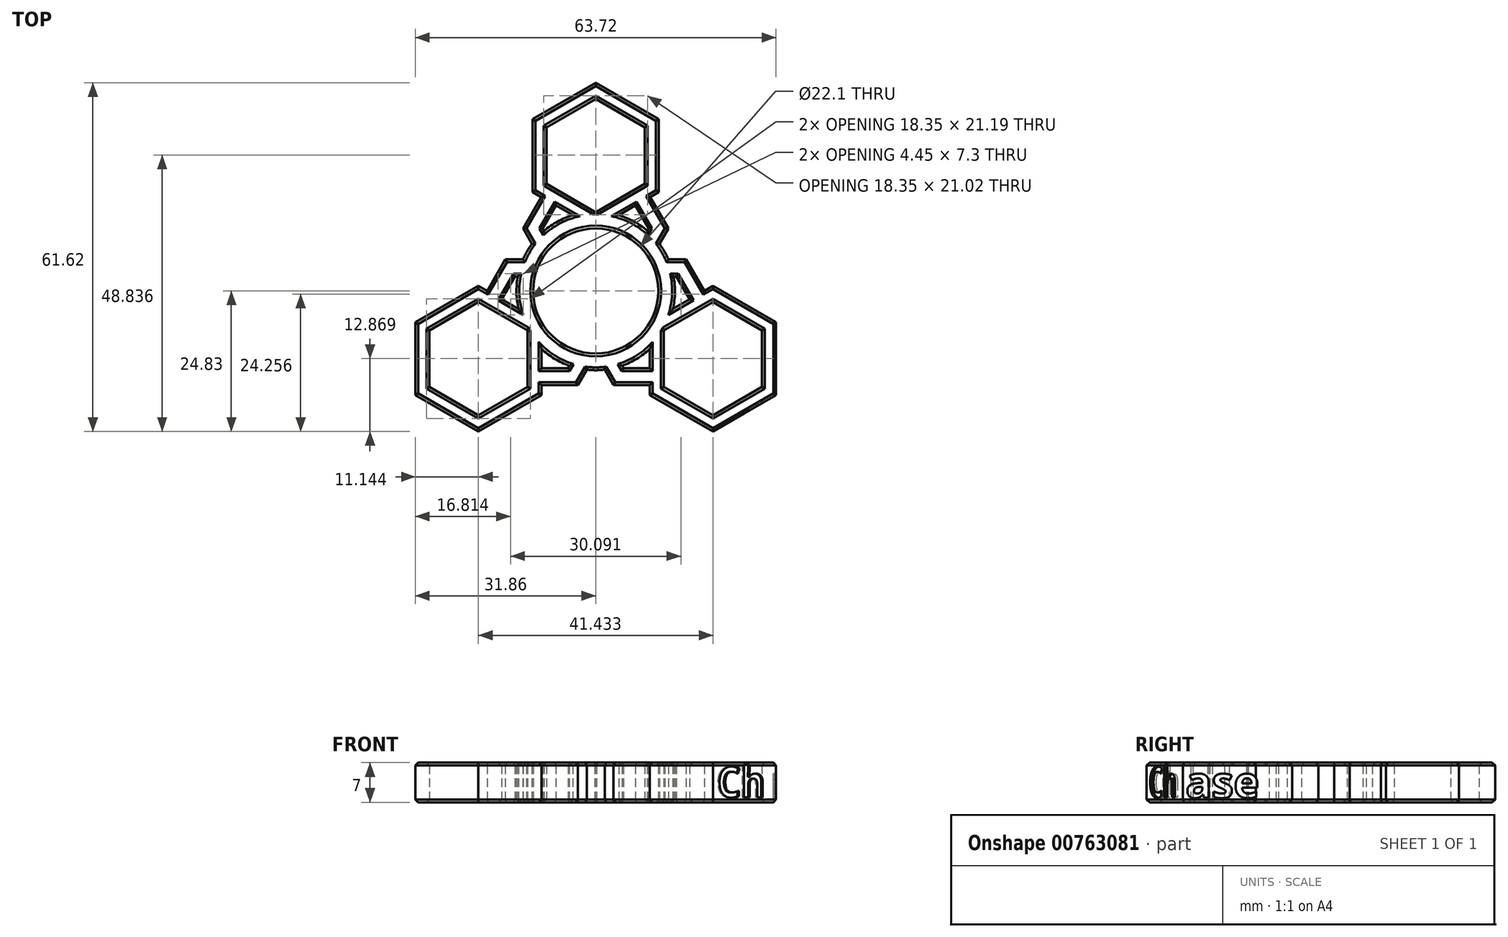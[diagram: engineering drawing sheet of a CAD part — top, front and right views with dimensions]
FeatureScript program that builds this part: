
annotation { "Feature Type Name" : "Feature", "Feature Type Description" : "" }
export const myFeature = defineFeature(function(context is Context, id is Id, definition is map)
    precondition{}
    {
        {
            var Q0;
            Q0=qCreatedBy(makeId("Top.planeOp"),FACE);
            var sketch = newSketch(context, id + "F0", { "sketchPlane" : qUnion([Q0])});
            skCircle(sketch, "E0", {"center": v(0, 0) * mm, "radius": 11.05 * mm});
            skCircle(sketch, "E1.cCircle", {"center": v(0, 23.92) * mm, "radius": 10.02 * mm, "construction": true});
            skLineSegment(sketch, "E1.0", {"start": v(0, 33.94) * mm, "end": v(8.68, 28.93) * mm});
            skLineSegment(sketch, "E1.1", {"start": v(8.67, 28.93) * mm, "end": v(8.68, 18.91) * mm});
            skLineSegment(sketch, "E1.2", {"start": v(8.67, 18.91) * mm, "end": v(0, 13.9) * mm});
            skLineSegment(sketch, "E1.3", {"start": v(0, 13.9) * mm, "end": v(-8.67, 18.91) * mm});
            skLineSegment(sketch, "E1.4", {"start": v(-8.67, 18.91) * mm, "end": v(-8.68, 28.93) * mm});
            skLineSegment(sketch, "E1.5", {"start": v(-8.67, 28.93) * mm, "end": v(0, 33.94) * mm});
            skCircle(sketch, "E2.cCircle", {"center": v(0, 11.05) * mm, "radius": 9.36 * mm, "construction": true});
            skLineSegment(sketch, "E2.0", {"start": v(9.36, 11.05) * mm, "end": v(4.68, 2.95) * mm});
            skLineSegment(sketch, "E2.1", {"start": v(4.68, 2.95) * mm, "end": v(-4.68, 2.95) * mm});
            skLineSegment(sketch, "E2.2", {"start": v(-4.68, 2.95) * mm, "end": v(-9.36, 11.05) * mm});
            skLineSegment(sketch, "E2.3", {"start": v(-9.36, 11.05) * mm, "end": v(-4.68, 19.15) * mm});
            skLineSegment(sketch, "E2.4", {"start": v(-4.68, 19.15) * mm, "end": v(4.68, 19.15) * mm});
            skLineSegment(sketch, "E2.5", {"start": v(4.68, 19.15) * mm, "end": v(9.36, 11.05) * mm});
            skLineSegment(sketch, "E3", {"start": v(0, 11.05) * mm, "end": v(30.07, 11.05) * mm, "construction": true});
            skLineSegment(sketch, "E4.0", {"start": v(-6.4, -0.05) * mm, "end": v(-12.82, 11.05) * mm});
            skLineSegment(sketch, "E4.1", {"start": v(-6.4, 22.15) * mm, "end": v(6.4, 22.15) * mm});
            skLineSegment(sketch, "E4.2", {"start": v(6.4, 22.15) * mm, "end": v(12.82, 11.05) * mm});
            skLineSegment(sketch, "E4.3", {"start": v(-12.82, 11.05) * mm, "end": v(-6.4, 22.15) * mm});
            skLineSegment(sketch, "E4.4", {"start": v(12.82, 11.05) * mm, "end": v(6.4, -0.05) * mm});
            skLineSegment(sketch, "E4.5", {"start": v(6.4, -0.05) * mm, "end": v(-6.4, -0.05) * mm});
            skCircle(sketch, "E5", {"center": v(0, 0) * mm, "radius": 14 * mm});
            skCircle(sketch, "E6.cCircle", {"center": v(0, 23.92) * mm, "radius": 12.87 * mm, "construction": true});
            skLineSegment(sketch, "E6.0", {"start": v(0, 11.05) * mm, "end": v(-11.15, 17.49) * mm});
            skLineSegment(sketch, "E6.1", {"start": v(-11.15, 17.49) * mm, "end": v(-11.15, 30.36) * mm});
            skLineSegment(sketch, "E6.2", {"start": v(-11.15, 30.36) * mm, "end": v(0, 36.8) * mm});
            skLineSegment(sketch, "E6.3", {"start": v(0, 36.8) * mm, "end": v(11.15, 30.36) * mm});
            skLineSegment(sketch, "E6.4", {"start": v(11.15, 30.36) * mm, "end": v(11.15, 17.49) * mm});
            skLineSegment(sketch, "E6.5", {"start": v(11.15, 17.49) * mm, "end": v(0, 11.05) * mm});
            skSolve(sketch);
        }
        {
            var Q0;
            {var subQ5=sQuery(id+"F0.wireOp",EDGE,"E1.0");Q0=makeQuery(id+"F0.imprint","IMPRINT",FACE,{"disambiguationData":[TD([[makeQuery(id+"F0.imprint","IMPRINT",EDGE,{"derivedFrom":subQ5}),1.0]])]});}
            var Q1;
            {var subQ1=sQuery(id+"F0.wireOp",EDGE,"E1.3");var subQ5=sQuery(id+"F0.wireOp",EDGE,"E1.4");var subQ6=makeQuery(id+"F0.imprint","INTERSECT",VERTEX,{"derivedFrom":[subQ1,subQ5]});Q1=makeQuery(id+"F0.imprint","IMPRINT",FACE,{"disambiguationData":[TD([[makeQuery(id+"F0.imprint","IMPRINT",EDGE,{"disambiguationData":[TD([[subQ6,1.0]])],"derivedFrom":subQ1}),1.0]])]});}
            var Q2;
            {var subQ1=sQuery(id+"F0.wireOp",EDGE,"E1.2");var subQ6=sQuery(id+"F0.wireOp",EDGE,"E1.3");var subQ13=makeQuery(id+"F0.imprint","INTERSECT",VERTEX,{"derivedFrom":[subQ1,subQ6]});Q2=makeQuery(id+"F0.imprint","IMPRINT",FACE,{"disambiguationData":[TD([[makeQuery(id+"F0.imprint","IMPRINT",EDGE,{"disambiguationData":[TD([[subQ13,1.0]])],"derivedFrom":subQ1}),1.0]])]});}
            var Q3;
            {var subQ3=sQuery(id+"F0.wireOp",EDGE,"E1.1");var subQ5=sQuery(id+"F0.wireOp",EDGE,"E1.2");var subQ6=makeQuery(id+"F0.imprint","INTERSECT",VERTEX,{"derivedFrom":[subQ3,subQ5]});Q3=makeQuery(id+"F0.imprint","IMPRINT",FACE,{"disambiguationData":[TD([[makeQuery(id+"F0.imprint","IMPRINT",EDGE,{"disambiguationData":[TD([[subQ6,1.0]])],"derivedFrom":subQ3}),1.0]])]});}
            var Q4;
            {var subQ5=sQuery(id+"F0.wireOp",EDGE,"E2.5");var subQ6=sQuery(id+"F0.wireOp",EDGE,"E2.0");var subQ7=makeQuery(id+"F0.imprint","INTERSECT",VERTEX,{"derivedFrom":[subQ6,subQ5]});Q4=makeQuery(id+"F0.imprint","IMPRINT",FACE,{"disambiguationData":[TD([[makeQuery(id+"F0.imprint","IMPRINT",EDGE,{"disambiguationData":[TD([[subQ7,-1.0]])],"derivedFrom":subQ6}),1.0]])]});}
            var Q5;
            {var subQ0=sQuery(id+"F0.wireOp",EDGE,"E2.0");var subQ1=sQuery(id+"F0.wireOp",EDGE,"E0");var subQ2=makeQuery(id+"F0.imprint","INTERSECT",VERTEX,{"derivedFrom":[subQ1,subQ0]});Q5=makeQuery(id+"F0.imprint","IMPRINT",FACE,{"disambiguationData":[TD([[makeQuery(id+"F0.imprint","IMPRINT",EDGE,{"disambiguationData":[TD([[subQ2,1.0]])],"derivedFrom":subQ1}),-1.0]])]});}
            var Q6;
            {var subQ1=sQuery(id+"F0.wireOp",EDGE,"E0");var subQ3=sQuery(id+"F0.wireOp",EDGE,"E2.0");var subQ4=makeQuery(id+"F0.imprint","INTERSECT",VERTEX,{"derivedFrom":[subQ1,subQ3]});Q6=makeQuery(id+"F0.imprint","IMPRINT",FACE,{"disambiguationData":[TD([[makeQuery(id+"F0.imprint","IMPRINT",EDGE,{"disambiguationData":[TD([[subQ4,1.0]])],"derivedFrom":subQ3}),-1.0]])]});}
            var Q7;
            {var subQ1=sQuery(id+"F0.wireOp",EDGE,"E0");var subQ3=sQuery(id+"F0.wireOp",EDGE,"E2.2");var subQ4=makeQuery(id+"F0.imprint","INTERSECT",VERTEX,{"derivedFrom":[subQ1,subQ3]});Q7=makeQuery(id+"F0.imprint","IMPRINT",FACE,{"disambiguationData":[TD([[makeQuery(id+"F0.imprint","IMPRINT",EDGE,{"disambiguationData":[TD([[subQ4,-1.0]])],"derivedFrom":subQ3}),-1.0]])]});}
            var Q8;
            {var subQ0=sQuery(id+"F0.wireOp",EDGE,"E6.5");var subQ1=sQuery(id+"F0.wireOp",EDGE,"E5");var subQ2=makeQuery(id+"F0.imprint","INTERSECT",VERTEX,{"derivedFrom":[subQ1,subQ0]});Q8=makeQuery(id+"F0.imprint","IMPRINT",FACE,{"disambiguationData":[TD([[makeQuery(id+"F0.imprint","IMPRINT",EDGE,{"disambiguationData":[TD([[subQ2,-1.0]])],"derivedFrom":subQ1}),1.0]])]});}
            var Q9;
            {var subQ0=sQuery(id+"F0.wireOp",EDGE,"E4.4");var subQ1=sQuery(id+"F0.wireOp",EDGE,"E0");var subQ2=makeQuery(id+"F0.imprint","INTERSECT",VERTEX,{"derivedFrom":[subQ1,subQ0]});Q9=makeQuery(id+"F0.imprint","IMPRINT",FACE,{"disambiguationData":[TD([[makeQuery(id+"F0.imprint","IMPRINT",EDGE,{"disambiguationData":[TD([[subQ2,1.0]])],"derivedFrom":subQ1}),-1.0]])]});}
            var Q10;
            {var subQ0=sQuery(id+"F0.wireOp",EDGE,"E2.2");var subQ1=sQuery(id+"F0.wireOp",EDGE,"E0");var subQ2=makeQuery(id+"F0.imprint","INTERSECT",VERTEX,{"derivedFrom":[subQ1,subQ0]});Q10=makeQuery(id+"F0.imprint","IMPRINT",FACE,{"disambiguationData":[TD([[makeQuery(id+"F0.imprint","IMPRINT",EDGE,{"disambiguationData":[TD([[subQ2,-1.0]])],"derivedFrom":subQ1}),-1.0]])]});}
            var Q11;
            {var subQ0=sQuery(id+"F0.wireOp",EDGE,"E2.3");var subQ1=sQuery(id+"F0.wireOp",EDGE,"E2.2");var subQ2=makeQuery(id+"F0.imprint","INTERSECT",VERTEX,{"derivedFrom":[subQ1,subQ0]});Q11=makeQuery(id+"F0.imprint","IMPRINT",FACE,{"disambiguationData":[TD([[makeQuery(id+"F0.imprint","IMPRINT",EDGE,{"disambiguationData":[TD([[subQ2,1.0]])],"derivedFrom":subQ1}),1.0]])]});}
            var Q12;
            {var subQ0=sQuery(id+"F0.wireOp",EDGE,"E5");var subQ1=sQuery(id+"F0.wireOp",EDGE,"E1.3");var subQ2=makeQuery(id+"F0.imprint","INTERSECT",VERTEX,{"derivedFrom":[subQ1,subQ0]});Q12=makeQuery(id+"F0.imprint","IMPRINT",FACE,{"disambiguationData":[TD([[makeQuery(id+"F0.imprint","IMPRINT",EDGE,{"disambiguationData":[TD([[subQ2,-1.0]])],"derivedFrom":subQ1}),1.0]])]});}
            var Q13;
            {var subQ0=sQuery(id+"F0.wireOp",EDGE,"E2.3");var subQ1=sQuery(id+"F0.wireOp",EDGE,"E1.3");var subQ2=makeQuery(id+"F0.imprint","INTERSECT",VERTEX,{"derivedFrom":[subQ1,subQ0]});Q13=makeQuery(id+"F0.imprint","IMPRINT",FACE,{"disambiguationData":[TD([[makeQuery(id+"F0.imprint","IMPRINT",EDGE,{"disambiguationData":[TD([[subQ2,-1.0]])],"derivedFrom":subQ1}),1.0]])]});}
            var Q14;
            {var subQ0=sQuery(id+"F0.wireOp",EDGE,"E4.2");var subQ1=sQuery(id+"F0.wireOp",EDGE,"E1.2");var subQ2=makeQuery(id+"F0.imprint","INTERSECT",VERTEX,{"derivedFrom":[subQ1,subQ0]});Q14=makeQuery(id+"F0.imprint","IMPRINT",FACE,{"disambiguationData":[TD([[makeQuery(id+"F0.imprint","IMPRINT",EDGE,{"disambiguationData":[TD([[subQ2,-1.0]])],"derivedFrom":subQ1}),1.0]])]});}
            var Q15;
            {var subQ0=sQuery(id+"F0.wireOp",EDGE,"E2.5");var subQ1=sQuery(id+"F0.wireOp",EDGE,"E1.2");var subQ2=makeQuery(id+"F0.imprint","INTERSECT",VERTEX,{"derivedFrom":[subQ1,subQ0]});Q15=makeQuery(id+"F0.imprint","IMPRINT",FACE,{"disambiguationData":[TD([[makeQuery(id+"F0.imprint","IMPRINT",EDGE,{"disambiguationData":[TD([[subQ2,-1.0]])],"derivedFrom":subQ1}),1.0]])]});}
            extrude(context, id + "F1", {"entities" : qUnion([Q0, Q1, Q2, Q3, Q4, Q5, Q6, Q7, Q8, Q9, Q10, Q11, Q12, Q13, Q14, Q15]), "depth" : 7 * mm, "offsetDistance" : 25 * mm});
        }
        {
            var Q0;
            Q0=qCreatedBy(makeId("Right.planeOp"),FACE);
            var sketch = newSketch(context, id + "F2", { "sketchPlane" : qUnion([Q0])});
            skLineSegment(sketch, "E7", {"start": v(0, 0) * mm, "end": v(0, 30.07) * mm});
            skSolve(sketch);
        }
        {
            var Q0;
            Q0=makeQuery(id+"F1.opExtrude","SWEPT_BODY",BODY,{"disambiguationData":[OSD([sQuery(id+"F0.wireOp",EDGE,"E0"),sQuery(id+"F0.wireOp",EDGE,"E1.0"),sQuery(id+"F0.wireOp",EDGE,"E1.1"),sQuery(id+"F0.wireOp",EDGE,"E1.2"),sQuery(id+"F0.wireOp",EDGE,"E1.3"),sQuery(id+"F0.wireOp",EDGE,"E1.4"),sQuery(id+"F0.wireOp",EDGE,"E1.5"),sQuery(id+"F0.wireOp",EDGE,"E2.0"),sQuery(id+"F0.wireOp",EDGE,"E2.2"),sQuery(id+"F0.wireOp",EDGE,"E2.3"),sQuery(id+"F0.wireOp",EDGE,"E2.5"),sQuery(id+"F0.wireOp",EDGE,"E4.0"),sQuery(id+"F0.wireOp",EDGE,"E4.2"),sQuery(id+"F0.wireOp",EDGE,"E4.3"),sQuery(id+"F0.wireOp",EDGE,"E4.4"),sQuery(id+"F0.wireOp",EDGE,"E5"),sQuery(id+"F0.wireOp",EDGE,"E6.0"),sQuery(id+"F0.wireOp",EDGE,"E6.1"),sQuery(id+"F0.wireOp",EDGE,"E6.2"),sQuery(id+"F0.wireOp",EDGE,"E6.3"),sQuery(id+"F0.wireOp",EDGE,"E6.4"),sQuery(id+"F0.wireOp",EDGE,"E6.5")])]});
            var Q1;
            Q1=sQuery(id+"F2.wireOp",EDGE,"E7");
            circularPattern(context, id + "F3", {"operationType" : NewBodyOperationType.ADD, "entities" : qUnion([Q0]), "axis" : qUnion([Q1]), "angle" : 360 * degree, "instanceCount" : 3, "equalSpace" : true});
        }
        {
            var Q0;
            Q0=makeQuery(id+"F3.opPattern","COPY",FACE,{"derivedFrom":makeQuery(id+"F1.opExtrude","SWEPT_FACE",FACE,{"disambiguationData":[OSD([sQuery(id+"F0.wireOp",EDGE,"E6.3")])]}),"instanceName":"2"});
            var sketch = newSketch(context, id + "F4", { "sketchPlane" : qUnion([Q0])});
            skText(sketch, "E8", { "text": "Ch", "fontName": "OpenSans-Bold.ttf"});
            const initialGuessF4  = {"E8": [0.00642, 0.00086, 1, 0, 0.00546]};
            skSetInitialGuess(sketch, initialGuessF4);
            skSolve(sketch);
        }
        {
            var Q0;
            Q0=makeQuery(id+"F3.opPattern","COPY",FACE,{"derivedFrom":makeQuery(id+"F1.opExtrude","SWEPT_FACE",FACE,{"disambiguationData":[OSD([sQuery(id+"F0.wireOp",EDGE,"E6.2")])]}),"instanceName":"2"});
            var sketch = newSketch(context, id + "F5", { "sketchPlane" : qUnion([Q0])});
            skText(sketch, "E9", { "text": "ase", "fontName": "OpenSans-Bold.ttf"});
            const initialGuessF5  = {"E9": [-0.01792, 0.00078, 1, 0, 0.00555]};
            skSetInitialGuess(sketch, initialGuessF5);
            skSolve(sketch);
        }
        {
            var Q0;
            Q0=qSketchRegion(id+"F4",true);
            extrude(context, id + "F6", {"entities" : qUnion([Q0]), "operationType" : NewBodyOperationType.REMOVE, "oppositeDirection" : true, "depth" : .5 * mm, "offsetDistance" : 25 * mm});
        }
        {
            var Q0;
            Q0=qSketchRegion(id+"F5",true);
            extrude(context, id + "F7", {"entities" : qUnion([Q0]), "operationType" : NewBodyOperationType.REMOVE, "oppositeDirection" : true, "depth" : .5 * mm, "offsetDistance" : 25 * mm});
        }
        {
            var Q0;
            Q0=makeQuery(id+"F3.opPattern","COPY",EDGE,{"derivedFrom":makeQuery(id+"F1.opExtrude","CAP_EDGE",EDGE,{"disambiguationData":[OSD([sQuery(id+"F0.wireOp",EDGE,"E6.1")])],"isStart":false}),"instanceName":"2"});
            var Q1;
            Q1=makeQuery(id+"F3.opPattern","COPY",EDGE,{"derivedFrom":makeQuery(id+"F1.opExtrude","CAP_EDGE",EDGE,{"disambiguationData":[OSD([sQuery(id+"F0.wireOp",EDGE,"E6.2")])],"isStart":false}),"instanceName":"2"});
            var Q2;
            Q2=makeQuery(id+"F3.opPattern","COPY",EDGE,{"derivedFrom":makeQuery(id+"F1.opExtrude","CAP_EDGE",EDGE,{"disambiguationData":[OSD([sQuery(id+"F0.wireOp",EDGE,"E6.3")])],"isStart":false}),"instanceName":"2"});
            var Q3;
            Q3=makeQuery(id+"F3.opPattern","COPY",EDGE,{"derivedFrom":makeQuery(id+"F1.opExtrude","CAP_EDGE",EDGE,{"disambiguationData":[OSD([sQuery(id+"F0.wireOp",EDGE,"E6.4")])],"isStart":false}),"instanceName":"2"});
            var Q4;
            {var subQ0=sQuery(id+"F0.wireOp",EDGE,"E6.5");Q4=makeQuery(id+"F3.opPattern","COPY",EDGE,{"derivedFrom":makeQuery(id+"F1.opExtrude","CAP_EDGE",EDGE,{"disambiguationData":[OSD([subQ0]),TDD([makeQuery(id+"F0.imprint","IMPRINT",EDGE,{"disambiguationData":[TD([[makeQuery(id+"F0.imprint","INTERSECT",VERTEX,{"derivedFrom":[sQuery(id+"F0.wireOp",EDGE,"E6.4"),subQ0]}),-1.0]])],"derivedFrom":subQ0})])],"isStart":false}),"instanceName":"2"});}
            var Q5;
            Q5=makeQuery(id+"F3.opPattern","COPY",EDGE,{"derivedFrom":makeQuery(id+"F1.opExtrude","CAP_EDGE",EDGE,{"disambiguationData":[OSD([sQuery(id+"F0.wireOp",EDGE,"E4.2")])],"isStart":false}),"instanceName":"2"});
            var Q6;
            Q6=makeQuery(id+"F3.opPattern","COPY",EDGE,{"derivedFrom":makeQuery(id+"F1.opExtrude","CAP_EDGE",EDGE,{"disambiguationData":[OSD([sQuery(id+"F0.wireOp",EDGE,"E4.4")])],"isStart":false}),"instanceName":"2"});
            var Q7;
            {var subQ0=sQuery(id+"F0.wireOp",EDGE,"E4.0");var subQ1=sQuery(id+"F0.wireOp",EDGE,"E5");var subQ4=makeQuery(id+"F0.imprint","IMPRINT",EDGE,{"disambiguationData":[TD([[makeQuery(id+"F0.imprint","INTERSECT",VERTEX,{"derivedFrom":[subQ0,subQ1]}),-1.0]])],"derivedFrom":subQ1});Q7=makeQuery(id+"F3.boolean.opBoolean","SPLIT",EDGE,{"disambiguationData":[TD([makeQuery(id+"F3.opPattern","COPY",FACE,{"derivedFrom":makeQuery(id+"F1.opExtrude","SWEPT_FACE",FACE,{"disambiguationData":[OSD([subQ0])]}),"instanceName":"1"})])],"derivedFrom":makeQuery(id+"F1.opExtrude","CAP_EDGE",EDGE,{"disambiguationData":[OSD([subQ1]),TDD([subQ4])],"isStart":false})});}
            var Q8;
            Q8=makeQuery(id+"F3.opPattern","COPY",EDGE,{"derivedFrom":makeQuery(id+"F1.opExtrude","CAP_EDGE",EDGE,{"disambiguationData":[OSD([sQuery(id+"F0.wireOp",EDGE,"E4.0")])],"isStart":false}),"instanceName":"1"});
            var Q9;
            Q9=makeQuery(id+"F3.opPattern","COPY",EDGE,{"derivedFrom":makeQuery(id+"F1.opExtrude","CAP_EDGE",EDGE,{"disambiguationData":[OSD([sQuery(id+"F0.wireOp",EDGE,"E4.3")])],"isStart":false}),"instanceName":"1"});
            var Q10;
            {var subQ0=makeQuery(id+"F1.opExtrude","CAP_FACE",FACE,{"disambiguationData":[OSD([sQuery(id+"F0.wireOp",EDGE,"E0"),sQuery(id+"F0.wireOp",EDGE,"E1.0"),sQuery(id+"F0.wireOp",EDGE,"E1.1"),sQuery(id+"F0.wireOp",EDGE,"E1.2"),sQuery(id+"F0.wireOp",EDGE,"E1.3"),sQuery(id+"F0.wireOp",EDGE,"E1.4"),sQuery(id+"F0.wireOp",EDGE,"E1.5"),sQuery(id+"F0.wireOp",EDGE,"E2.0"),sQuery(id+"F0.wireOp",EDGE,"E2.2"),sQuery(id+"F0.wireOp",EDGE,"E2.3"),sQuery(id+"F0.wireOp",EDGE,"E2.5"),sQuery(id+"F0.wireOp",EDGE,"E4.0"),sQuery(id+"F0.wireOp",EDGE,"E4.2"),sQuery(id+"F0.wireOp",EDGE,"E4.3"),sQuery(id+"F0.wireOp",EDGE,"E4.4"),sQuery(id+"F0.wireOp",EDGE,"E5"),sQuery(id+"F0.wireOp",EDGE,"E6.0"),sQuery(id+"F0.wireOp",EDGE,"E6.1"),sQuery(id+"F0.wireOp",EDGE,"E6.2"),sQuery(id+"F0.wireOp",EDGE,"E6.3"),sQuery(id+"F0.wireOp",EDGE,"E6.4"),sQuery(id+"F0.wireOp",EDGE,"E6.5")])],"isStart":false});Q10=makeQuery(id+"F3.boolean.opBoolean","MERGE",FACE,{"derivedFrom":[subQ0,makeQuery(id+"F3.opPattern","COPY",FACE,{"derivedFrom":subQ0,"instanceName":"1"}),makeQuery(id+"F3.opPattern","COPY",FACE,{"derivedFrom":subQ0,"instanceName":"2"})]});}
            var Q11;
            {var subQ0=makeQuery(id+"F1.opExtrude","CAP_FACE",FACE,{"disambiguationData":[OSD([sQuery(id+"F0.wireOp",EDGE,"E0"),sQuery(id+"F0.wireOp",EDGE,"E1.0"),sQuery(id+"F0.wireOp",EDGE,"E1.1"),sQuery(id+"F0.wireOp",EDGE,"E1.2"),sQuery(id+"F0.wireOp",EDGE,"E1.3"),sQuery(id+"F0.wireOp",EDGE,"E1.4"),sQuery(id+"F0.wireOp",EDGE,"E1.5"),sQuery(id+"F0.wireOp",EDGE,"E2.0"),sQuery(id+"F0.wireOp",EDGE,"E2.2"),sQuery(id+"F0.wireOp",EDGE,"E2.3"),sQuery(id+"F0.wireOp",EDGE,"E2.5"),sQuery(id+"F0.wireOp",EDGE,"E4.0"),sQuery(id+"F0.wireOp",EDGE,"E4.2"),sQuery(id+"F0.wireOp",EDGE,"E4.3"),sQuery(id+"F0.wireOp",EDGE,"E4.4"),sQuery(id+"F0.wireOp",EDGE,"E5"),sQuery(id+"F0.wireOp",EDGE,"E6.0"),sQuery(id+"F0.wireOp",EDGE,"E6.1"),sQuery(id+"F0.wireOp",EDGE,"E6.2"),sQuery(id+"F0.wireOp",EDGE,"E6.3"),sQuery(id+"F0.wireOp",EDGE,"E6.4"),sQuery(id+"F0.wireOp",EDGE,"E6.5")])],"isStart":true});Q11=makeQuery(id+"F3.boolean.opBoolean","MERGE",FACE,{"derivedFrom":[subQ0,makeQuery(id+"F3.opPattern","COPY",FACE,{"derivedFrom":subQ0,"instanceName":"1"}),makeQuery(id+"F3.opPattern","COPY",FACE,{"derivedFrom":subQ0,"instanceName":"2"})]});}
            chamfer(context, id + "F8", {"entities" : qUnion([Q0, Q1, Q2, Q3, Q4, Q5, Q6, Q7, Q8, Q9, Q10, Q11]), "width" : .5 * mm, "tangentPropagation" : true});
        }
    });
